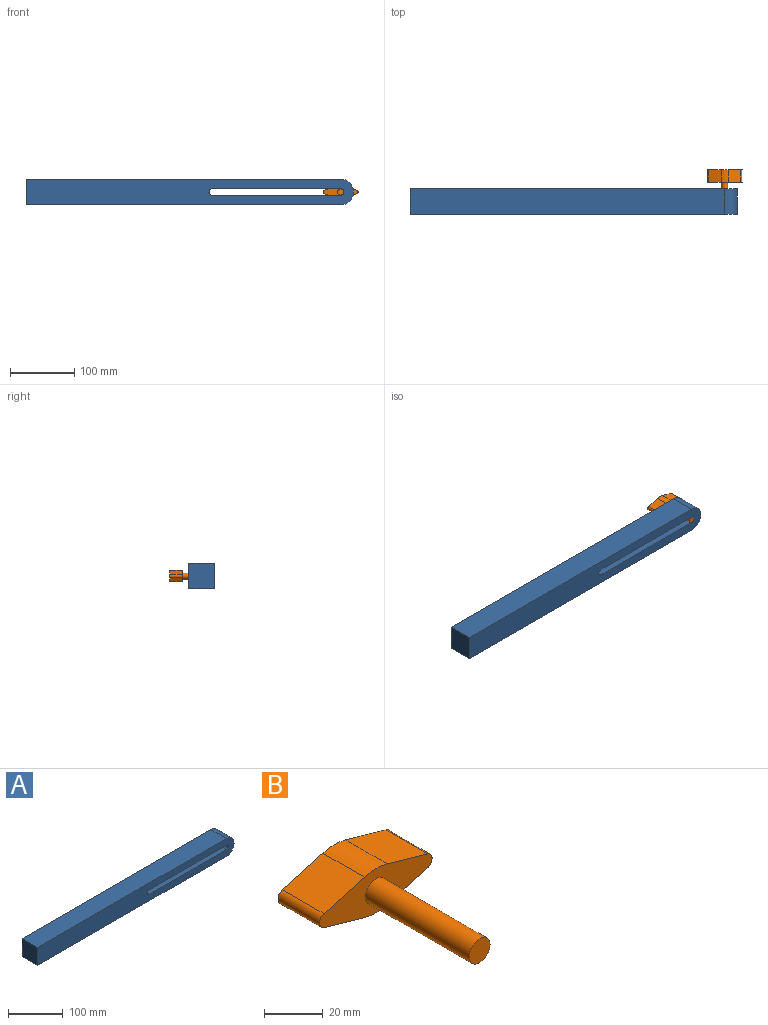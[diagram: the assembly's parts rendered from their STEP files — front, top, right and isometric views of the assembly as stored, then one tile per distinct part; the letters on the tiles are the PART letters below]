
ASSEMBLY  parts=2 mates=1
PART A: 10 faces, bbox 510x40x40 mm
  f0: plane 490x40mm, normal (0,0,1), area 19600mm2, adj f1,f7,f8,f9
  f1: plane 40x40mm, normal (-1,0,0), area 1600mm2, adj f0,f2,f8,f9
  f2: plane 490x40mm, normal (0,0,-1), area 19600mm2, adj f1,f7,f8,f9
  f3: cylinder r=5mm len=40mm, axis (0,1,0), area 628.3mm2, adj f4,f6,f8,f9
  f4: plane 200x40mm, normal (0,0,1), area 8000mm2, adj f3,f5,f8,f9
  f5: cylinder r=5mm len=40mm, axis (0,1,0), area 628.3mm2, adj f4,f6,f8,f9
  f6: plane 200x40mm, normal (0,0,-1), area 8000mm2, adj f3,f5,f8,f9
  f7: cylinder r=20mm len=40mm, axis (0,1,0), area 2513.3mm2, adj f0,f2,f8,f9
  f8: plane 510x40mm, normal (0,-1,0), area 18149.8mm2, adj f0,f1,f2,f3,f4,f5,f6,f7
  f9: plane 510x40mm, normal (0,1,0), area 18149.8mm2, adj f0,f1,f2,f3,f4,f5,f6,f7
PART B: 12 faces, bbox 54.2x70x18.4 mm
  f0: cylinder r=20mm len=20mm, axis (0,1,0), area 222.6mm2, adj f1,f7,f8,f9
  f1: plane 20x19.41mm, normal (0.27,0,-0.96), area 403.7mm2, adj f0,f2,f8,f9
  f2: cylinder r=3mm len=20mm, axis (0,1,0), area 155.1mm2, adj f1,f3,f8,f9
  f3: plane 20x19.41mm, normal (0.27,0,0.96), area 403.7mm2, adj f2,f4,f8,f9
  f4: cylinder r=20mm len=20mm, axis (0,1,0), area 222.6mm2, adj f3,f5,f8,f9
  f5: plane 20x19.41mm, normal (-0.27,0,0.96), area 403.7mm2, adj f4,f6,f8,f9
  f6: cylinder r=3mm len=20mm, axis (0,1,0), area 155.1mm2, adj f5,f7,f8,f9
  f7: plane 20x19.41mm, normal (-0.27,0,-0.96), area 403.7mm2, adj f0,f6,f8,f9
  f8: plane 54.16x18.4mm, normal (0,-1,0), area 575.8mm2, adj f0,f1,f2,f3,f4,f5,f6,f7
  f9: plane 54.16x18.4mm, normal (0,1,0), area 654.3mm2, adj f0,f1,f2,f3,f4,f5,f6,f7
  f10: cylinder r=5mm len=50mm, axis (0,1,0), area 1570.8mm2, adj f8,f11
  f11: plane 10x10mm, normal (0,-1,0), area 78.5mm2, adj f10
PLACE A t=(39.06,186.64,136.93)mm
PLACE B t=(274.06,216.64,136.93)mm fixed
MATE pin_slot A.f7 <-> B.f10  axis (0,-1,0) through (274.06,146.64,136.93)mm
